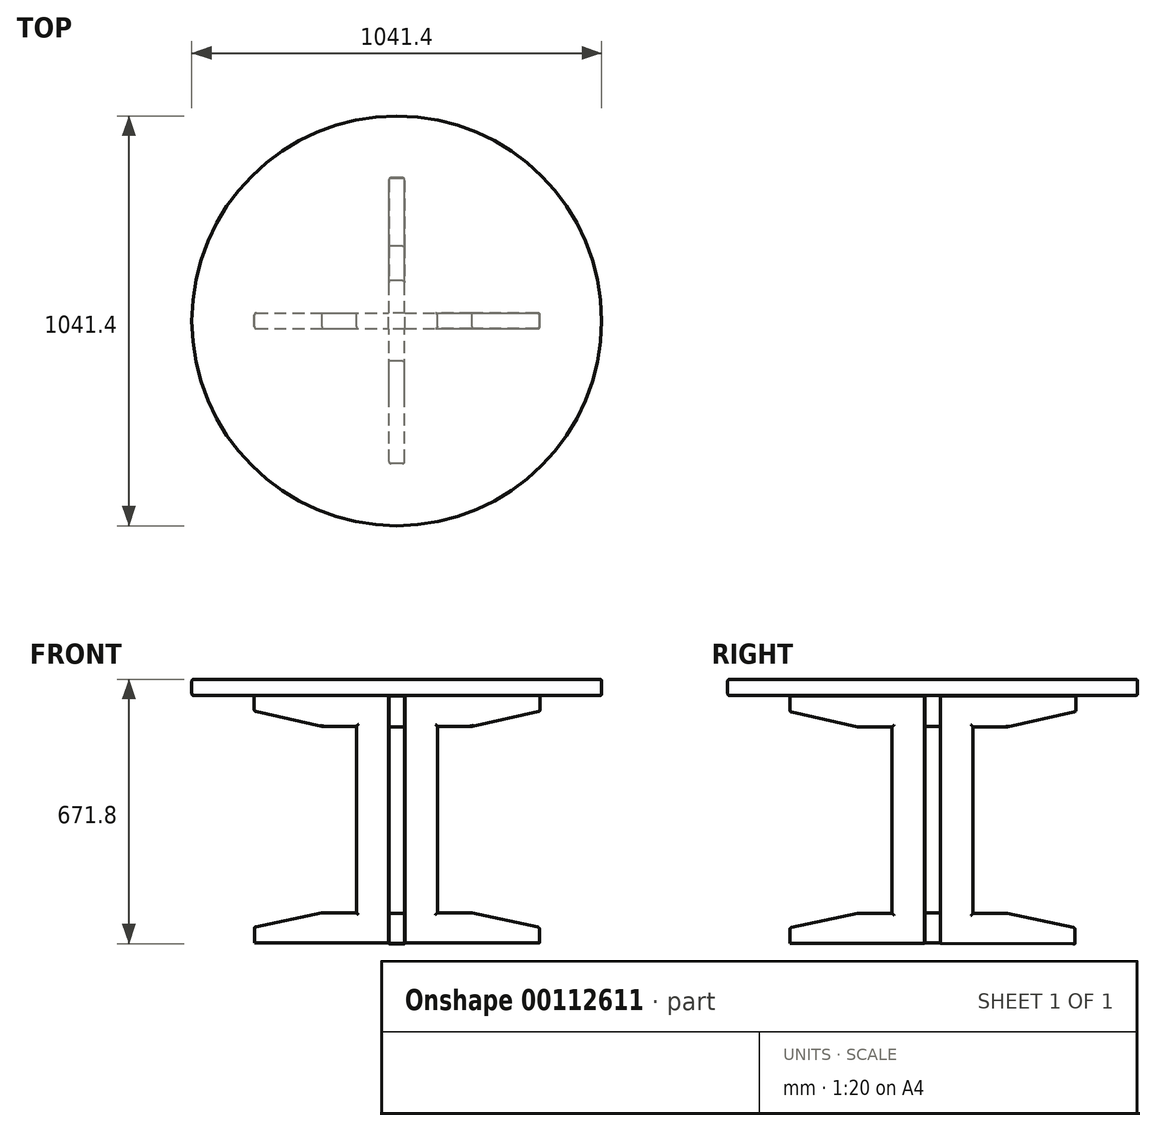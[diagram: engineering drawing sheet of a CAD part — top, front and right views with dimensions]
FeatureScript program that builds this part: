
annotation { "Feature Type Name" : "Feature", "Feature Type Description" : "" }
export const myFeature = defineFeature(function(context is Context, id is Id, definition is map)
    precondition{}
    {
        {
            var Q0;
            Q0=qCreatedBy(makeId("Top.planeOp"),FACE);
            var sketch = newSketch(context, id + "F0", { "sketchPlane" : qUnion([Q0])});
            skCircle(sketch, "E0", {"center": v(0, 0) * mm, "radius": 520.7 * mm});
            skLineSegment(sketch, "E1.bottom", {"start": v(20.64, 361.95) * mm, "end": v(-20.64, 361.95) * mm});
            skLineSegment(sketch, "E1.top", {"start": v(20.64, -361.95) * mm, "end": v(-20.64, -361.95) * mm});
            skLineSegment(sketch, "E1.left", {"start": v(20.64, 361.95) * mm, "end": v(20.64, -361.95) * mm});
            skLineSegment(sketch, "E1.right", {"start": v(-20.64, 361.95) * mm, "end": v(-20.64, -361.95) * mm});
            skLineSegment(sketch, "E2.bottom", {"start": v(-361.95, 20.64) * mm, "end": v(361.95, 20.64) * mm});
            skLineSegment(sketch, "E2.top", {"start": v(-361.95, -20.64) * mm, "end": v(361.95, -20.64) * mm});
            skLineSegment(sketch, "E2.left", {"start": v(-361.95, 20.64) * mm, "end": v(-361.95, -20.64) * mm});
            skLineSegment(sketch, "E2.right", {"start": v(361.95, 20.64) * mm, "end": v(361.95, -20.64) * mm});
            skPoint(sketch, "E3", {"position": v(-520.7, 0) * mm});
            skPoint(sketch, "E4", {"position": v(520.7, 0) * mm});
            skLineSegment(sketch, "E5.bottom", {"start": v(105.64, -20.64) * mm, "end": v(-105.64, -20.64) * mm});
            skLineSegment(sketch, "E5.top", {"start": v(105.64, 20.64) * mm, "end": v(-105.64, 20.64) * mm});
            skLineSegment(sketch, "E5.left", {"start": v(105.64, -20.64) * mm, "end": v(105.64, 20.64) * mm});
            skLineSegment(sketch, "E5.right", {"start": v(-105.64, -20.64) * mm, "end": v(-105.64, 20.64) * mm});
            skLineSegment(sketch, "E6.bottom", {"start": v(20.64, -105.64) * mm, "end": v(-20.64, -105.64) * mm});
            skLineSegment(sketch, "E6.top", {"start": v(20.64, 105.64) * mm, "end": v(-20.64, 105.64) * mm});
            skLineSegment(sketch, "E6.left", {"start": v(20.64, -105.64) * mm, "end": v(20.64, 105.64) * mm});
            skLineSegment(sketch, "E6.right", {"start": v(-20.64, -105.64) * mm, "end": v(-20.64, 105.64) * mm});
            skSolve(sketch);
        }
        {
            var Q0;
            Q0=makeQuery(id+"F0.imprint","IMPRINT",FACE,{"disambiguationData":[TD([[makeQuery(id+"F0.imprint","IMPRINT",EDGE,{"derivedFrom":sQuery(id+"F0.wireOp",EDGE,"E0")}),1.0]])]});
            var Q1;
            {var subQ0=sQuery(id+"F0.wireOp",EDGE,"E1.right");var subQ1=sQuery(id+"F0.wireOp",EDGE,"b60915dd-e518-4b98-8b0a-9520b7d790ac");var subQ2=makeQuery(id+"F0.imprint","INTERSECT",VERTEX,{"disambiguationData":[OD(0.0)],"derivedFrom":[subQ1,subQ0]});Q1=makeQuery(id+"F0.imprint","IMPRINT",FACE,{"disambiguationData":[TD([[makeQuery(id+"F0.imprint","IMPRINT",EDGE,{"disambiguationData":[TD([[subQ2,-1.0]])],"derivedFrom":subQ1}),1.0]])]});}
            var Q2;
            {var subQ0=sQuery(id+"F0.wireOp",EDGE,"E2.bottom");var subQ1=sQuery(id+"F0.wireOp",EDGE,"b60915dd-e518-4b98-8b0a-9520b7d790ac");var subQ2=makeQuery(id+"F0.imprint","INTERSECT",VERTEX,{"disambiguationData":[OD(0.0)],"derivedFrom":[subQ1,subQ0]});Q2=makeQuery(id+"F0.imprint","IMPRINT",FACE,{"disambiguationData":[TD([[makeQuery(id+"F0.imprint","IMPRINT",EDGE,{"disambiguationData":[TD([[subQ2,-1.0]])],"derivedFrom":subQ1}),1.0]])]});}
            var Q3;
            {var subQ0=sQuery(id+"F0.wireOp",EDGE,"E2.top");var subQ1=sQuery(id+"F0.wireOp",EDGE,"b60915dd-e518-4b98-8b0a-9520b7d790ac");var subQ2=makeQuery(id+"F0.imprint","INTERSECT",VERTEX,{"disambiguationData":[OD(0.0)],"derivedFrom":[subQ1,subQ0]});Q3=makeQuery(id+"F0.imprint","IMPRINT",FACE,{"disambiguationData":[TD([[makeQuery(id+"F0.imprint","IMPRINT",EDGE,{"disambiguationData":[TD([[subQ2,-1.0]])],"derivedFrom":subQ1}),1.0]])]});}
            var Q4;
            {var subQ0=sQuery(id+"F0.wireOp",EDGE,"E1.left");var subQ1=sQuery(id+"F0.wireOp",EDGE,"b60915dd-e518-4b98-8b0a-9520b7d790ac");var subQ2=makeQuery(id+"F0.imprint","INTERSECT",VERTEX,{"disambiguationData":[OD(0.0)],"derivedFrom":[subQ1,subQ0]});Q4=makeQuery(id+"F0.imprint","IMPRINT",FACE,{"disambiguationData":[TD([[makeQuery(id+"F0.imprint","IMPRINT",EDGE,{"disambiguationData":[TD([[subQ2,1.0]])],"derivedFrom":subQ1}),1.0]])]});}
            var Q5;
            {var subQ1=sQuery(id+"F0.wireOp",EDGE,"E1.bottom");Q5=makeQuery(id+"F0.imprint","IMPRINT",FACE,{"disambiguationData":[TD([[makeQuery(id+"F0.imprint","IMPRINT",EDGE,{"derivedFrom":subQ1}),1.0]])]});}
            var Q6;
            {var subQ5=sQuery(id+"F0.wireOp",EDGE,"E2.left");Q6=makeQuery(id+"F0.imprint","IMPRINT",FACE,{"disambiguationData":[TD([[makeQuery(id+"F0.imprint","IMPRINT",EDGE,{"derivedFrom":subQ5}),1.0]])]});}
            var Q7;
            {var subQ1=sQuery(id+"F0.wireOp",EDGE,"E1.top");Q7=makeQuery(id+"F0.imprint","IMPRINT",FACE,{"disambiguationData":[TD([[makeQuery(id+"F0.imprint","IMPRINT",EDGE,{"derivedFrom":subQ1}),-1.0]])]});}
            var Q8;
            {var subQ5=sQuery(id+"F0.wireOp",EDGE,"E2.right");Q8=makeQuery(id+"F0.imprint","IMPRINT",FACE,{"disambiguationData":[TD([[makeQuery(id+"F0.imprint","IMPRINT",EDGE,{"derivedFrom":subQ5}),-1.0]])]});}
            var Q9;
            {var subQ0=sQuery(id+"F0.wireOp",EDGE,"E2.bottom");var subQ1=sQuery(id+"F0.wireOp",EDGE,"E1.left");var subQ2=makeQuery(id+"F0.imprint","INTERSECT",VERTEX,{"derivedFrom":[subQ1,subQ0]});Q9=makeQuery(id+"F0.imprint","IMPRINT",FACE,{"disambiguationData":[TD([[makeQuery(id+"F0.imprint","IMPRINT",EDGE,{"disambiguationData":[TD([[subQ2,-1.0]])],"derivedFrom":subQ1}),-1.0]])]});}
            var Q10;
            {var subQ5=sQuery(id+"F0.wireOp",EDGE,"E6.top");Q10=makeQuery(id+"F0.imprint","IMPRINT",FACE,{"disambiguationData":[TD([[makeQuery(id+"F0.imprint","IMPRINT",EDGE,{"derivedFrom":subQ5}),1.0]])]});}
            var Q11;
            {var subQ0=sQuery(id+"F0.wireOp",EDGE,"E5.left");Q11=makeQuery(id+"F0.imprint","IMPRINT",FACE,{"disambiguationData":[TD([[makeQuery(id+"F0.imprint","IMPRINT",EDGE,{"derivedFrom":subQ0}),1.0]])]});}
            var Q12;
            {var subQ0=sQuery(id+"F0.wireOp",EDGE,"E6.left");var subQ1=sQuery(id+"F0.wireOp",EDGE,"E5.bottom");var subQ2=makeQuery(id+"F0.imprint","INTERSECT",VERTEX,{"derivedFrom":[subQ1,subQ0]});Q12=makeQuery(id+"F0.imprint","IMPRINT",FACE,{"disambiguationData":[TD([[makeQuery(id+"F0.imprint","IMPRINT",EDGE,{"disambiguationData":[TD([[subQ2,-1.0]])],"derivedFrom":subQ1}),-1.0]])]});}
            var Q13;
            {var subQ5=sQuery(id+"F0.wireOp",EDGE,"E6.bottom");Q13=makeQuery(id+"F0.imprint","IMPRINT",FACE,{"disambiguationData":[TD([[makeQuery(id+"F0.imprint","IMPRINT",EDGE,{"derivedFrom":subQ5}),-1.0]])]});}
            var Q14;
            {var subQ0=sQuery(id+"F0.wireOp",EDGE,"E5.right");Q14=makeQuery(id+"F0.imprint","IMPRINT",FACE,{"disambiguationData":[TD([[makeQuery(id+"F0.imprint","IMPRINT",EDGE,{"derivedFrom":subQ0}),-1.0]])]});}
            extrude(context, id + "F1", {"entities" : qUnion([Q0, Q1, Q2, Q3, Q4, Q5, Q6, Q7, Q8, Q9, Q10, Q11, Q12, Q13, Q14]), "depth" : 41.27 * mm});
        }
        {
            var Q0;
            Q0=qCreatedBy(makeId("Front.planeOp"),FACE);
            var sketch = newSketch(context, id + "F2", { "sketchPlane" : qUnion([Q0])});
            skLineSegment(sketch, "E7.bottom", {"start": v(20.55, 0) * mm, "end": v(190.55, 0) * mm});
            skLineSegment(sketch, "E7.top", {"start": v(20.55, -552.45) * mm, "end": v(190.55, -552.45) * mm});
            skLineSegment(sketch, "E7.left", {"start": v(20.55, 0) * mm, "end": v(20.55, -552.45) * mm});
            skLineSegment(sketch, "E7.right", {"start": v(190.55, 0) * mm, "end": v(190.55, -78.13) * mm});
            skLineSegment(sketch, "E8.bottom", {"start": v(-190.27, 0) * mm, "end": v(-20.27, 0) * mm});
            skLineSegment(sketch, "E8.top", {"start": v(-190.27, -551.88) * mm, "end": v(-20.27, -551.88) * mm});
            skLineSegment(sketch, "E8.left", {"start": v(-190.27, 0) * mm, "end": v(-190.27, -78.06) * mm});
            skLineSegment(sketch, "E8.right", {"start": v(-20.27, 0) * mm, "end": v(-20.27, -551.88) * mm});
            skLineSegment(sketch, "E9", {"start": v(190.55, 0) * mm, "end": v(364.05, 0) * mm});
            skLineSegment(sketch, "E10", {"start": v(364.05, 0) * mm, "end": v(364.05, -40) * mm});
            skLineSegment(sketch, "E11", {"start": v(-190.27, 0) * mm, "end": v(-362.04, 0) * mm});
            skLineSegment(sketch, "E12", {"start": v(-362.04, 0) * mm, "end": v(-362.04, -40) * mm});
            skLineSegment(sketch, "E13", {"start": v(-362.04, 0) * mm, "end": v(-20.27, 0) * mm});
            skLineSegment(sketch, "E14", {"start": v(20.55, 0) * mm, "end": v(364.05, 0) * mm});
            skLineSegment(sketch, "E15", {"start": v(-362.04, -40) * mm, "end": v(-190.27, -78.06) * mm});
            skLineSegment(sketch, "E16", {"start": v(190.55, -78.13) * mm, "end": v(364.05, -40) * mm});
            skLineSegment(sketch, "E17", {"start": v(-361.81, -588.7) * mm, "end": v(-361.81, -628.7) * mm});
            skLineSegment(sketch, "E18", {"start": v(362.15, -589.02) * mm, "end": v(362.15, -629.02) * mm});
            skLineSegment(sketch, "E19", {"start": v(-361.81, -588.7) * mm, "end": v(-190.27, -551.88) * mm});
            skLineSegment(sketch, "E20", {"start": v(-361.81, -628.7) * mm, "end": v(362.15, -629.02) * mm});
            skLineSegment(sketch, "E21", {"start": v(362.15, -589.02) * mm, "end": v(190.55, -552.45) * mm});
            skLineSegment(sketch, "E22", {"start": v(-20.27, -551.88) * mm, "end": v(-20.27, -628.84) * mm});
            skLineSegment(sketch, "E23", {"start": v(20.55, -552.45) * mm, "end": v(20.55, -628.86) * mm});
            skLineSegment(sketch, "E24", {"start": v(190.55, -78.13) * mm, "end": v(20.55, -78.13) * mm});
            skLineSegment(sketch, "E25", {"start": v(-190.27, -78.06) * mm, "end": v(-20.27, -78.06) * mm});
            skLineSegment(sketch, "E26", {"start": v(-190.27, -551.88) * mm, "end": v(-190.27, -628.77) * mm});
            skLineSegment(sketch, "E27", {"start": v(190.55, -552.45) * mm, "end": v(190.55, -628.94) * mm});
            skLineSegment(sketch, "E28", {"start": v(-102.77, -78.06) * mm, "end": v(-102.77, -551.88) * mm});
            skLineSegment(sketch, "E29", {"start": v(103.05, -78.13) * mm, "end": v(103.05, -552.45) * mm});
            skSolve(sketch);
        }
        {
            var Q0;
            {var subQ0=sQuery(id+"F2.wireOp",EDGE,"E17");Q0=makeQuery(id+"F2.imprint","IMPRINT",FACE,{"disambiguationData":[TD([[makeQuery(id+"F2.imprint","IMPRINT",EDGE,{"derivedFrom":subQ0}),1.0]])]});}
            var Q1;
            Q1=makeQuery(id+"F2.imprint","IMPRINT",FACE,{"disambiguationData":[TD([[makeQuery(id+"F2.imprint","IMPRINT",EDGE,{"derivedFrom":sQuery(id+"F2.wireOp",EDGE,"E8.top")}),-1.0]])]});
            var Q2;
            Q2=makeQuery(id+"F2.imprint","IMPRINT",FACE,{"disambiguationData":[TD([[makeQuery(id+"F2.imprint","IMPRINT",EDGE,{"derivedFrom":sQuery(id+"F2.wireOp",EDGE,"E7.top")}),-1.0]])]});
            var Q3;
            {var subQ0=sQuery(id+"F2.wireOp",EDGE,"E18");Q3=makeQuery(id+"F2.imprint","IMPRINT",FACE,{"disambiguationData":[TD([[makeQuery(id+"F2.imprint","IMPRINT",EDGE,{"derivedFrom":subQ0}),-1.0]])]});}
            var Q4;
            {var subQ0=sQuery(id+"F2.wireOp",EDGE,"E7.right");Q4=makeQuery(id+"F2.imprint","IMPRINT",FACE,{"disambiguationData":[TD([[makeQuery(id+"F2.imprint","IMPRINT",EDGE,{"derivedFrom":subQ0}),1.0]])]});}
            var Q5;
            {var subQ1=sQuery(id+"F2.wireOp",EDGE,"E7.right");Q5=makeQuery(id+"F2.imprint","IMPRINT",FACE,{"disambiguationData":[TD([[makeQuery(id+"F2.imprint","IMPRINT",EDGE,{"derivedFrom":subQ1}),-1.0]])]});}
            var Q6;
            {var subQ1=sQuery(id+"F2.wireOp",EDGE,"E8.left");Q6=makeQuery(id+"F2.imprint","IMPRINT",FACE,{"disambiguationData":[TD([[makeQuery(id+"F2.imprint","IMPRINT",EDGE,{"derivedFrom":subQ1}),1.0]])]});}
            var Q7;
            {var subQ0=sQuery(id+"F2.wireOp",EDGE,"E8.left");Q7=makeQuery(id+"F2.imprint","IMPRINT",FACE,{"disambiguationData":[TD([[makeQuery(id+"F2.imprint","IMPRINT",EDGE,{"derivedFrom":subQ0}),-1.0]])]});}
            var Q8;
            {var subQ3=sQuery(id+"F2.wireOp",EDGE,"E28");Q8=makeQuery(id+"F2.imprint","IMPRINT",FACE,{"disambiguationData":[TD([[makeQuery(id+"F2.imprint","IMPRINT",EDGE,{"derivedFrom":subQ3}),1.0]])]});}
            var Q9;
            {var subQ3=sQuery(id+"F2.wireOp",EDGE,"E29");Q9=makeQuery(id+"F2.imprint","IMPRINT",FACE,{"disambiguationData":[TD([[makeQuery(id+"F2.imprint","IMPRINT",EDGE,{"derivedFrom":subQ3}),-1.0]])]});}
            extrude(context, id + "F3", {"entities" : qUnion([Q0, Q1, Q2, Q3, Q4, Q5, Q6, Q7, Q8, Q9]), "endBound" : BoundingType.SYMMETRIC, "depth" : 40 * mm});
        }
        {
            var Q0;
            Q0=qCreatedBy(makeId("Right.planeOp"),FACE);
            var sketch = newSketch(context, id + "F4", { "sketchPlane" : qUnion([Q0])});
            skLineSegment(sketch, "E30.bottom", {"start": v(20, -1.5) * mm, "end": v(190, -1.5) * mm});
            skLineSegment(sketch, "E30.top", {"start": v(20, -553.95) * mm, "end": v(190, -553.95) * mm});
            skLineSegment(sketch, "E30.left", {"start": v(20, -1.5) * mm, "end": v(20, -553.95) * mm});
            skLineSegment(sketch, "E30.right", {"start": v(190, -1.5) * mm, "end": v(190, -79.63) * mm});
            skLineSegment(sketch, "E31.bottom", {"start": v(-190.34, -1.5) * mm, "end": v(-20.34, -1.5) * mm});
            skLineSegment(sketch, "E31.top", {"start": v(-190.34, -553.28) * mm, "end": v(-20.34, -553.28) * mm});
            skLineSegment(sketch, "E31.left", {"start": v(-190.34, -1.5) * mm, "end": v(-190.34, -79.67) * mm});
            skLineSegment(sketch, "E31.right", {"start": v(-20.34, -1.5) * mm, "end": v(-20.34, -553.28) * mm});
            skLineSegment(sketch, "E32", {"start": v(190, -1.5) * mm, "end": v(363.5, -1.5) * mm});
            skLineSegment(sketch, "E33", {"start": v(363.5, -1.5) * mm, "end": v(363.5, -41.5) * mm});
            skLineSegment(sketch, "E34", {"start": v(-190.34, -1.5) * mm, "end": v(-362.58, -1.5) * mm});
            skLineSegment(sketch, "E35", {"start": v(-362.58, -1.5) * mm, "end": v(-362.58, -41.5) * mm});
            skLineSegment(sketch, "E36", {"start": v(-362.58, -1.5) * mm, "end": v(-20.34, -1.5) * mm});
            skLineSegment(sketch, "E37", {"start": v(20, -1.5) * mm, "end": v(363.5, -1.5) * mm});
            skLineSegment(sketch, "E38", {"start": v(-362.58, -41.5) * mm, "end": v(-190.34, -79.67) * mm});
            skLineSegment(sketch, "E39", {"start": v(190, -79.63) * mm, "end": v(363.5, -41.5) * mm});
            skLineSegment(sketch, "E40", {"start": v(-362.35, -590.2) * mm, "end": v(-362.35, -630.2) * mm});
            skLineSegment(sketch, "E41", {"start": v(361.61, -590.52) * mm, "end": v(361.61, -630.52) * mm});
            skLineSegment(sketch, "E42", {"start": v(-362.35, -590.2) * mm, "end": v(-190.34, -553.28) * mm});
            skLineSegment(sketch, "E43", {"start": v(-362.35, -630.2) * mm, "end": v(361.61, -630.52) * mm});
            skLineSegment(sketch, "E44", {"start": v(361.61, -590.52) * mm, "end": v(190, -553.95) * mm});
            skLineSegment(sketch, "E45", {"start": v(-20.34, -553.28) * mm, "end": v(-20.34, -630.35) * mm});
            skLineSegment(sketch, "E46", {"start": v(20, -553.95) * mm, "end": v(20, -630.37) * mm});
            skLineSegment(sketch, "E47", {"start": v(190, -79.63) * mm, "end": v(20, -79.63) * mm});
            skLineSegment(sketch, "E48", {"start": v(-190.34, -79.67) * mm, "end": v(-20.34, -79.67) * mm});
            skLineSegment(sketch, "E49", {"start": v(-190.34, -553.28) * mm, "end": v(-190.34, -630.27) * mm});
            skLineSegment(sketch, "E50", {"start": v(190, -553.95) * mm, "end": v(190, -630.44) * mm});
            skLineSegment(sketch, "E51", {"start": v(-102.84, -79.67) * mm, "end": v(-102.84, -553.28) * mm});
            skLineSegment(sketch, "E52", {"start": v(102.5, -79.63) * mm, "end": v(102.5, -553.95) * mm});
            skSolve(sketch);
        }
        {
            var Q0;
            {var subQ0=sQuery(id+"F4.wireOp",EDGE,"E46");Q0=makeQuery(id+"F4.imprint","IMPRINT",FACE,{"disambiguationData":[TD([[makeQuery(id+"F4.imprint","IMPRINT",EDGE,{"derivedFrom":subQ0}),1.0]])]});}
            var Q1;
            {var subQ0=sQuery(id+"F4.wireOp",EDGE,"E41");Q1=makeQuery(id+"F4.imprint","IMPRINT",FACE,{"disambiguationData":[TD([[makeQuery(id+"F4.imprint","IMPRINT",EDGE,{"derivedFrom":subQ0}),-1.0]])]});}
            var Q2;
            {var subQ0=sQuery(id+"F4.wireOp",EDGE,"E45");Q2=makeQuery(id+"F4.imprint","IMPRINT",FACE,{"disambiguationData":[TD([[makeQuery(id+"F4.imprint","IMPRINT",EDGE,{"derivedFrom":subQ0}),-1.0]])]});}
            var Q3;
            {var subQ0=sQuery(id+"F4.wireOp",EDGE,"E40");Q3=makeQuery(id+"F4.imprint","IMPRINT",FACE,{"disambiguationData":[TD([[makeQuery(id+"F4.imprint","IMPRINT",EDGE,{"derivedFrom":subQ0}),1.0]])]});}
            var Q4;
            {var subQ1=sQuery(id+"F4.wireOp",EDGE,"E30.right");Q4=makeQuery(id+"F4.imprint","IMPRINT",FACE,{"disambiguationData":[TD([[makeQuery(id+"F4.imprint","IMPRINT",EDGE,{"derivedFrom":subQ1}),-1.0]])]});}
            var Q5;
            {var subQ0=sQuery(id+"F4.wireOp",EDGE,"E30.right");Q5=makeQuery(id+"F4.imprint","IMPRINT",FACE,{"disambiguationData":[TD([[makeQuery(id+"F4.imprint","IMPRINT",EDGE,{"derivedFrom":subQ0}),1.0]])]});}
            var Q6;
            {var subQ1=sQuery(id+"F4.wireOp",EDGE,"E31.left");Q6=makeQuery(id+"F4.imprint","IMPRINT",FACE,{"disambiguationData":[TD([[makeQuery(id+"F4.imprint","IMPRINT",EDGE,{"derivedFrom":subQ1}),1.0]])]});}
            var Q7;
            {var subQ0=sQuery(id+"F4.wireOp",EDGE,"E31.left");Q7=makeQuery(id+"F4.imprint","IMPRINT",FACE,{"disambiguationData":[TD([[makeQuery(id+"F4.imprint","IMPRINT",EDGE,{"derivedFrom":subQ0}),-1.0]])]});}
            var Q8;
            {var subQ3=sQuery(id+"F4.wireOp",EDGE,"E52");Q8=makeQuery(id+"F4.imprint","IMPRINT",FACE,{"disambiguationData":[TD([[makeQuery(id+"F4.imprint","IMPRINT",EDGE,{"derivedFrom":subQ3}),-1.0]])]});}
            var Q9;
            {var subQ3=sQuery(id+"F4.wireOp",EDGE,"E51");Q9=makeQuery(id+"F4.imprint","IMPRINT",FACE,{"disambiguationData":[TD([[makeQuery(id+"F4.imprint","IMPRINT",EDGE,{"derivedFrom":subQ3}),1.0]])]});}
            extrude(context, id + "F5", {"entities" : qUnion([Q0, Q1, Q2, Q3, Q4, Q5, Q6, Q7, Q8, Q9]), "operationType" : NewBodyOperationType.ADD, "endBound" : BoundingType.SYMMETRIC, "depth" : 40 * mm});
        }
        {
            var Q0;
            Q0=makeQuery(id+"F1.opExtrude","CAP_EDGE",EDGE,{"disambiguationData":[OSD([sQuery(id+"F0.wireOp",EDGE,"E0")])],"isStart":false});
            var Q1;
            Q1=makeQuery(id+"F1.opExtrude","CAP_EDGE",EDGE,{"disambiguationData":[OSD([sQuery(id+"F0.wireOp",EDGE,"E0")])],"isStart":true});
            var Q2;
            Q2=makeQuery(id+"F3.opExtrude","CAP_EDGE",EDGE,{"disambiguationData":[OSD([sQuery(id+"F2.wireOp",EDGE,"E16")])],"isStart":false});
            var Q3;
            Q3=makeQuery(id+"F3.opExtrude","CAP_EDGE",EDGE,{"disambiguationData":[OSD([sQuery(id+"F2.wireOp",EDGE,"E24")])],"isStart":false});
            var Q4;
            Q4=makeQuery(id+"F3.opExtrude","CAP_EDGE",EDGE,{"disambiguationData":[OSD([sQuery(id+"F2.wireOp",EDGE,"E10")])],"isStart":false});
            var Q5;
            Q5=makeQuery(id+"F3.opExtrude","CAP_EDGE",EDGE,{"disambiguationData":[OSD([sQuery(id+"F2.wireOp",EDGE,"E10")])],"isStart":true});
            var Q6;
            Q6=makeQuery(id+"F3.opExtrude","SWEPT_EDGE",EDGE,{"disambiguationData":[OSD([sQuery(id+"F2.wireOp",EDGE,"E10"),sQuery(id+"F2.wireOp",EDGE,"E16")])]});
            var Q7;
            Q7=makeQuery(id+"F3.opExtrude","CAP_EDGE",EDGE,{"disambiguationData":[OSD([sQuery(id+"F2.wireOp",EDGE,"E16")])],"isStart":true});
            var Q8;
            Q8=makeQuery(id+"F3.opExtrude","CAP_EDGE",EDGE,{"disambiguationData":[OSD([sQuery(id+"F2.wireOp",EDGE,"E24")])],"isStart":true});
            var Q9;
            Q9=makeQuery(id+"F3.opExtrude","CAP_EDGE",EDGE,{"disambiguationData":[OSD([sQuery(id+"F2.wireOp",EDGE,"E29")])],"isStart":true});
            var Q10;
            Q10=makeQuery(id+"F3.opExtrude","CAP_EDGE",EDGE,{"disambiguationData":[OSD([sQuery(id+"F2.wireOp",EDGE,"E29")])],"isStart":false});
            var Q11;
            Q11=makeQuery(id+"F5.opExtrude","CAP_EDGE",EDGE,{"disambiguationData":[OSD([sQuery(id+"F4.wireOp",EDGE,"E47")])],"isStart":false});
            var Q12;
            Q12=makeQuery(id+"F5.opExtrude","CAP_EDGE",EDGE,{"disambiguationData":[OSD([sQuery(id+"F4.wireOp",EDGE,"E52")])],"isStart":false});
            var Q13;
            Q13=makeQuery(id+"F5.opExtrude","CAP_EDGE",EDGE,{"disambiguationData":[OSD([sQuery(id+"F4.wireOp",EDGE,"E39")])],"isStart":false});
            var Q14;
            Q14=makeQuery(id+"F5.opExtrude","CAP_EDGE",EDGE,{"disambiguationData":[OSD([sQuery(id+"F4.wireOp",EDGE,"E33")])],"isStart":false});
            var Q15;
            Q15=makeQuery(id+"F5.opExtrude","CAP_EDGE",EDGE,{"disambiguationData":[OSD([sQuery(id+"F4.wireOp",EDGE,"E33")])],"isStart":true});
            var Q16;
            Q16=makeQuery(id+"F5.opExtrude","CAP_EDGE",EDGE,{"disambiguationData":[OSD([sQuery(id+"F4.wireOp",EDGE,"E39")])],"isStart":true});
            var Q17;
            Q17=makeQuery(id+"F5.opExtrude","CAP_EDGE",EDGE,{"disambiguationData":[OSD([sQuery(id+"F4.wireOp",EDGE,"E47")])],"isStart":true});
            var Q18;
            Q18=makeQuery(id+"F5.opExtrude","CAP_EDGE",EDGE,{"disambiguationData":[OSD([sQuery(id+"F4.wireOp",EDGE,"E52")])],"isStart":true});
            var Q19;
            Q19=makeQuery(id+"F5.opExtrude","CAP_EDGE",EDGE,{"disambiguationData":[OSD([sQuery(id+"F4.wireOp",EDGE,"E30.top")])],"isStart":false});
            var Q20;
            Q20=makeQuery(id+"F5.opExtrude","CAP_EDGE",EDGE,{"disambiguationData":[OSD([sQuery(id+"F4.wireOp",EDGE,"E44")])],"isStart":false});
            var Q21;
            Q21=makeQuery(id+"F5.opExtrude","CAP_EDGE",EDGE,{"disambiguationData":[OSD([sQuery(id+"F4.wireOp",EDGE,"E41")])],"isStart":true});
            var Q22;
            Q22=makeQuery(id+"F5.opExtrude","SWEPT_EDGE",EDGE,{"disambiguationData":[OSD([sQuery(id+"F4.wireOp",EDGE,"E41"),sQuery(id+"F4.wireOp",EDGE,"E44")])]});
            var Q23;
            Q23=makeQuery(id+"F5.opExtrude","CAP_EDGE",EDGE,{"disambiguationData":[OSD([sQuery(id+"F4.wireOp",EDGE,"E41")])],"isStart":false});
            var Q24;
            Q24=makeQuery(id+"F3.opExtrude","CAP_EDGE",EDGE,{"disambiguationData":[OSD([sQuery(id+"F2.wireOp",EDGE,"E19")])],"isStart":true});
            var Q25;
            Q25=makeQuery(id+"F3.opExtrude","CAP_EDGE",EDGE,{"disambiguationData":[OSD([sQuery(id+"F2.wireOp",EDGE,"E8.top")])],"isStart":true});
            var Q26;
            Q26=makeQuery(id+"F3.opExtrude","CAP_EDGE",EDGE,{"disambiguationData":[OSD([sQuery(id+"F2.wireOp",EDGE,"E28")])],"isStart":true});
            var Q27;
            Q27=makeQuery(id+"F3.opExtrude","CAP_EDGE",EDGE,{"disambiguationData":[OSD([sQuery(id+"F2.wireOp",EDGE,"E25")])],"isStart":true});
            var Q28;
            Q28=makeQuery(id+"F3.opExtrude","CAP_EDGE",EDGE,{"disambiguationData":[OSD([sQuery(id+"F2.wireOp",EDGE,"E15")])],"isStart":true});
            var Q29;
            Q29=makeQuery(id+"F3.opExtrude","CAP_EDGE",EDGE,{"disambiguationData":[OSD([sQuery(id+"F2.wireOp",EDGE,"E15")])],"isStart":false});
            var Q30;
            Q30=makeQuery(id+"F3.opExtrude","CAP_EDGE",EDGE,{"disambiguationData":[OSD([sQuery(id+"F2.wireOp",EDGE,"E25")])],"isStart":false});
            var Q31;
            Q31=makeQuery(id+"F3.opExtrude","CAP_EDGE",EDGE,{"disambiguationData":[OSD([sQuery(id+"F2.wireOp",EDGE,"E12")])],"isStart":true});
            var Q32;
            Q32=makeQuery(id+"F3.opExtrude","CAP_EDGE",EDGE,{"disambiguationData":[OSD([sQuery(id+"F2.wireOp",EDGE,"E17")])],"isStart":true});
            var Q33;
            Q33=makeQuery(id+"F3.opExtrude","CAP_EDGE",EDGE,{"disambiguationData":[OSD([sQuery(id+"F2.wireOp",EDGE,"E17")])],"isStart":false});
            var Q34;
            Q34=makeQuery(id+"F3.opExtrude","SWEPT_EDGE",EDGE,{"disambiguationData":[OSD([sQuery(id+"F2.wireOp",EDGE,"E17"),sQuery(id+"F2.wireOp",EDGE,"E19")])]});
            var Q35;
            Q35=makeQuery(id+"F3.opExtrude","SWEPT_EDGE",EDGE,{"disambiguationData":[OSD([sQuery(id+"F2.wireOp",EDGE,"E12"),sQuery(id+"F2.wireOp",EDGE,"E15")])]});
            var Q36;
            Q36=makeQuery(id+"F3.opExtrude","CAP_EDGE",EDGE,{"disambiguationData":[OSD([sQuery(id+"F2.wireOp",EDGE,"E12")])],"isStart":false});
            var Q37;
            Q37=makeQuery(id+"F3.opExtrude","CAP_EDGE",EDGE,{"disambiguationData":[OSD([sQuery(id+"F2.wireOp",EDGE,"E7.top")])],"isStart":false});
            var Q38;
            Q38=makeQuery(id+"F3.opExtrude","CAP_EDGE",EDGE,{"disambiguationData":[OSD([sQuery(id+"F2.wireOp",EDGE,"E21")])],"isStart":false});
            var Q39;
            Q39=makeQuery(id+"F5.opExtrude","CAP_EDGE",EDGE,{"disambiguationData":[OSD([sQuery(id+"F4.wireOp",EDGE,"E51")])],"isStart":false});
            var Q40;
            Q40=makeQuery(id+"F5.opExtrude","CAP_EDGE",EDGE,{"disambiguationData":[OSD([sQuery(id+"F4.wireOp",EDGE,"E51")])],"isStart":true});
            var Q41;
            Q41=makeQuery(id+"F5.opExtrude","CAP_EDGE",EDGE,{"disambiguationData":[OSD([sQuery(id+"F4.wireOp",EDGE,"E48")])],"isStart":false});
            var Q42;
            Q42=makeQuery(id+"F5.opExtrude","CAP_EDGE",EDGE,{"disambiguationData":[OSD([sQuery(id+"F4.wireOp",EDGE,"E48")])],"isStart":true});
            var Q43;
            Q43=makeQuery(id+"F5.opExtrude","SWEPT_EDGE",EDGE,{"disambiguationData":[OSD([sQuery(id+"F4.wireOp",EDGE,"E31.left"),sQuery(id+"F4.wireOp",EDGE,"E38"),sQuery(id+"F4.wireOp",EDGE,"E48")])]});
            var Q44;
            Q44=makeQuery(id+"F5.opExtrude","CAP_EDGE",EDGE,{"disambiguationData":[OSD([sQuery(id+"F4.wireOp",EDGE,"E38")])],"isStart":false});
            var Q45;
            Q45=makeQuery(id+"F5.opExtrude","CAP_EDGE",EDGE,{"disambiguationData":[OSD([sQuery(id+"F4.wireOp",EDGE,"E38")])],"isStart":true});
            var Q46;
            Q46=makeQuery(id+"F5.opExtrude","CAP_EDGE",EDGE,{"disambiguationData":[OSD([sQuery(id+"F4.wireOp",EDGE,"E42")])],"isStart":false});
            var Q47;
            Q47=makeQuery(id+"F5.opExtrude","CAP_EDGE",EDGE,{"disambiguationData":[OSD([sQuery(id+"F4.wireOp",EDGE,"E31.top")])],"isStart":false});
            var Q48;
            Q48=makeQuery(id+"F5.opExtrude","CAP_EDGE",EDGE,{"disambiguationData":[OSD([sQuery(id+"F4.wireOp",EDGE,"E40")])],"isStart":false});
            var Q49;
            Q49=makeQuery(id+"F5.opExtrude","SWEPT_EDGE",EDGE,{"disambiguationData":[OSD([sQuery(id+"F4.wireOp",EDGE,"E40"),sQuery(id+"F4.wireOp",EDGE,"E42")])]});
            var Q50;
            Q50=makeQuery(id+"F5.opExtrude","CAP_EDGE",EDGE,{"disambiguationData":[OSD([sQuery(id+"F4.wireOp",EDGE,"E40")])],"isStart":true});
            var Q51;
            Q51=makeQuery(id+"F3.opExtrude","CAP_EDGE",EDGE,{"disambiguationData":[OSD([sQuery(id+"F2.wireOp",EDGE,"E18")])],"isStart":true});
            var Q52;
            Q52=makeQuery(id+"F3.opExtrude","CAP_EDGE",EDGE,{"disambiguationData":[OSD([sQuery(id+"F2.wireOp",EDGE,"E18")])],"isStart":false});
            var Q53;
            Q53=makeQuery(id+"F3.opExtrude","SWEPT_EDGE",EDGE,{"disambiguationData":[OSD([sQuery(id+"F2.wireOp",EDGE,"E18"),sQuery(id+"F2.wireOp",EDGE,"E21")])]});
            var Q54;
            Q54=makeQuery(id+"F3.opExtrude","CAP_EDGE",EDGE,{"disambiguationData":[OSD([sQuery(id+"F2.wireOp",EDGE,"E21")])],"isStart":true});
            var Q55;
            Q55=makeQuery(id+"F5.opExtrude","CAP_EDGE",EDGE,{"disambiguationData":[OSD([sQuery(id+"F4.wireOp",EDGE,"E44")])],"isStart":true});
            var Q56;
            Q56=makeQuery(id+"F5.opExtrude","CAP_EDGE",EDGE,{"disambiguationData":[OSD([sQuery(id+"F4.wireOp",EDGE,"E30.top")])],"isStart":true});
            var Q57;
            Q57=makeQuery(id+"F5.opExtrude","SWEPT_EDGE",EDGE,{"disambiguationData":[OSD([sQuery(id+"F4.wireOp",EDGE,"E30.top"),sQuery(id+"F4.wireOp",EDGE,"E44"),sQuery(id+"F4.wireOp",EDGE,"E50")])]});
            var Q58;
            Q58=makeQuery(id+"F3.opExtrude","CAP_EDGE",EDGE,{"disambiguationData":[OSD([sQuery(id+"F2.wireOp",EDGE,"E7.top")])],"isStart":true});
            var Q59;
            Q59=makeQuery(id+"F3.opExtrude","SWEPT_EDGE",EDGE,{"disambiguationData":[OSD([sQuery(id+"F2.wireOp",EDGE,"E7.top"),sQuery(id+"F2.wireOp",EDGE,"E21"),sQuery(id+"F2.wireOp",EDGE,"E27")])]});
            var Q60;
            Q60=makeQuery(id+"F3.opExtrude","CAP_EDGE",EDGE,{"disambiguationData":[OSD([sQuery(id+"F2.wireOp",EDGE,"E19")])],"isStart":false});
            var Q61;
            Q61=makeQuery(id+"F3.opExtrude","CAP_EDGE",EDGE,{"disambiguationData":[OSD([sQuery(id+"F2.wireOp",EDGE,"E8.top")])],"isStart":false});
            var Q62;
            Q62=makeQuery(id+"F3.opExtrude","SWEPT_EDGE",EDGE,{"disambiguationData":[OSD([sQuery(id+"F2.wireOp",EDGE,"E8.top"),sQuery(id+"F2.wireOp",EDGE,"E19"),sQuery(id+"F2.wireOp",EDGE,"E26")])]});
            var Q63;
            Q63=makeQuery(id+"F5.opExtrude","CAP_EDGE",EDGE,{"disambiguationData":[OSD([sQuery(id+"F4.wireOp",EDGE,"E31.top")])],"isStart":true});
            var Q64;
            Q64=makeQuery(id+"F5.opExtrude","CAP_EDGE",EDGE,{"disambiguationData":[OSD([sQuery(id+"F4.wireOp",EDGE,"E42")])],"isStart":true});
            var Q65;
            Q65=makeQuery(id+"F5.opExtrude","SWEPT_EDGE",EDGE,{"disambiguationData":[OSD([sQuery(id+"F4.wireOp",EDGE,"E31.top"),sQuery(id+"F4.wireOp",EDGE,"E42"),sQuery(id+"F4.wireOp",EDGE,"E49")])]});
            var Q66;
            Q66=makeQuery(id+"F3.opExtrude","CAP_EDGE",EDGE,{"disambiguationData":[OSD([sQuery(id+"F2.wireOp",EDGE,"E28")])],"isStart":false});
            var Q67;
            Q67=makeQuery(id+"F5.opExtrude","SWEPT_EDGE",EDGE,{"disambiguationData":[OSD([sQuery(id+"F4.wireOp",EDGE,"E33"),sQuery(id+"F4.wireOp",EDGE,"E39")])]});
            var Q68;
            Q68=makeQuery(id+"F5.opExtrude","SWEPT_EDGE",EDGE,{"disambiguationData":[OSD([sQuery(id+"F4.wireOp",EDGE,"E35"),sQuery(id+"F4.wireOp",EDGE,"E38")])]});
            var Q69;
            Q69=makeQuery(id+"F5.opExtrude","CAP_EDGE",EDGE,{"disambiguationData":[OSD([sQuery(id+"F4.wireOp",EDGE,"E35")])],"isStart":false});
            var Q70;
            Q70=makeQuery(id+"F5.opExtrude","CAP_EDGE",EDGE,{"disambiguationData":[OSD([sQuery(id+"F4.wireOp",EDGE,"E35")])],"isStart":true});
            fillet(context, id + "F6", {"entities" : qUnion([Q0, Q1, Q2, Q3, Q4, Q5, Q6, Q7, Q8, Q9, Q10, Q11, Q12, Q13, Q14, Q15, Q16, Q17, Q18, Q19, Q20, Q21, Q22, Q23, Q24, Q25, Q26, Q27, Q28, Q29, Q30, Q31, Q32, Q33, Q34, Q35, Q36, Q37, Q38, Q39, Q40, Q41, Q42, Q43, Q44, Q45, Q46, Q47, Q48, Q49, Q50, Q51, Q52, Q53, Q54, Q55, Q56, Q57, Q58, Q59, Q60, Q61, Q62, Q63, Q64, Q65, Q66, Q67, Q68, Q69, Q70]), "radius" : 5.08 * mm, "tangentPropagation" : true, "allowEdgeOverflow" : false});
        }
    });
